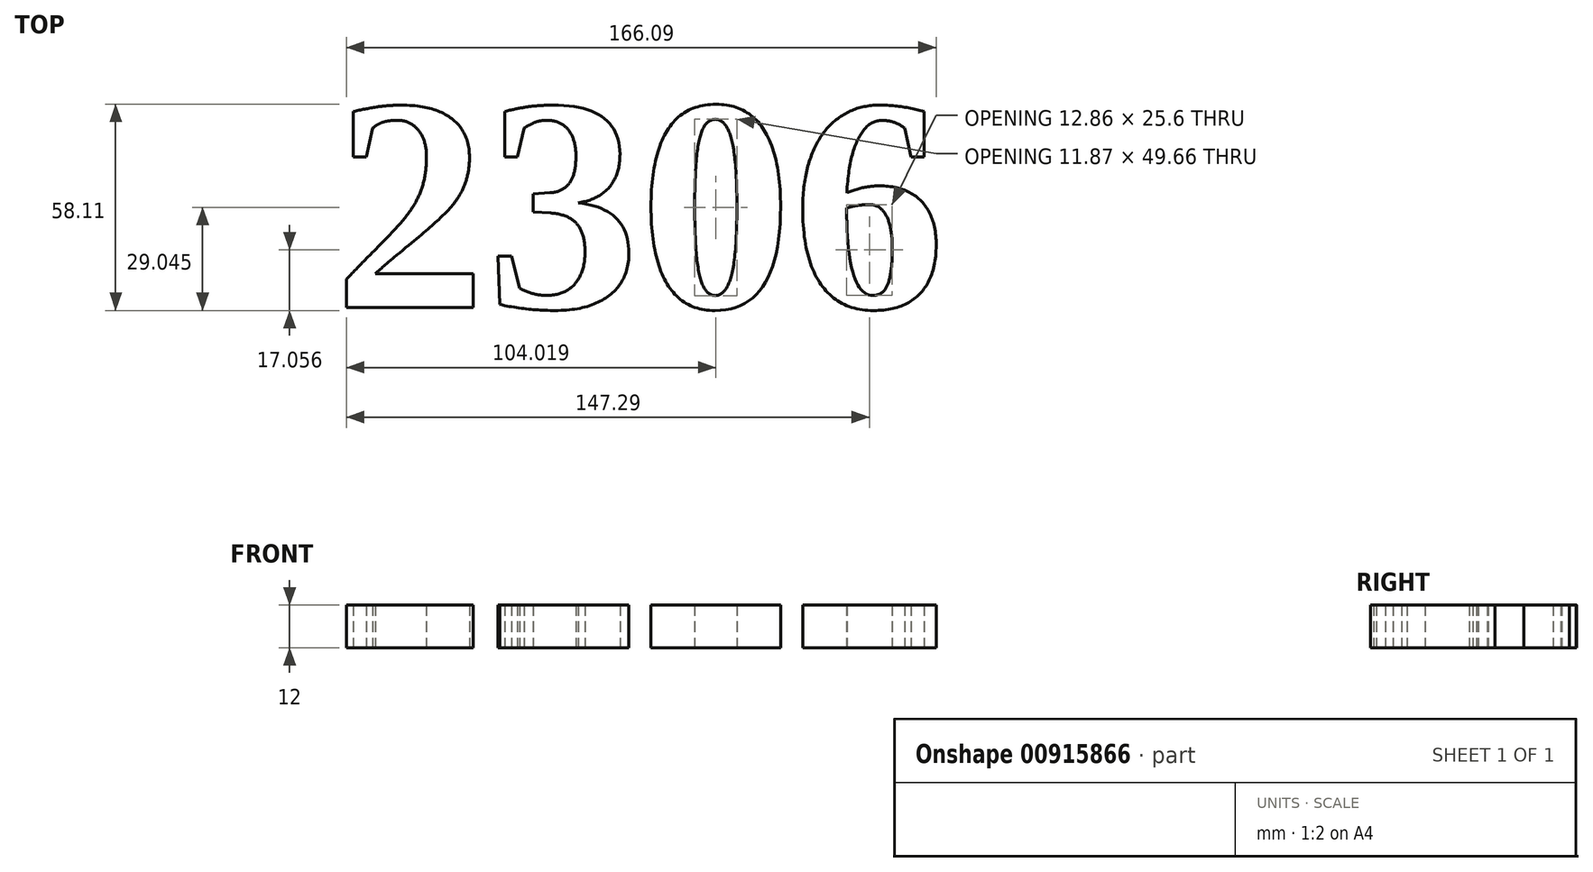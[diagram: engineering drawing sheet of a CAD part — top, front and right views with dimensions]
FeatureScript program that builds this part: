
annotation { "Feature Type Name" : "Feature", "Feature Type Description" : "" }
export const myFeature = defineFeature(function(context is Context, id is Id, definition is map)
    precondition{}
    {
        {
            var Q0;
            Q0=qCreatedBy(makeId("Top.planeOp"),FACE);
            var sketch = newSketch(context, id + "F0", { "sketchPlane" : qUnion([Q0])});
            skText(sketch, "E0", { "text": "2306", "fontName": "Tinos-Bold.ttf"});
            const initialGuessF0  = {"E0": [-0.08754, -0.0306, 1, 0, 0.062]};
            skSetInitialGuess(sketch, initialGuessF0);
            skSolve(sketch);
        }
        {
            var Q0;
            Q0=makeQuery(id+"F0.imprint","IMPRINT",FACE,{"disambiguationData":[TD([[makeQuery(id+"F0.imprint","IMPRINT",EDGE,{"derivedFrom":sQuery(id+"F0.wireOp",EDGE,"E0.sketch_text.stroke-0")}),-1.0]])]});
            var Q1;
            Q1=makeQuery(id+"F0.imprint","IMPRINT",FACE,{"disambiguationData":[TD([[makeQuery(id+"F0.imprint","IMPRINT",EDGE,{"derivedFrom":sQuery(id+"F0.wireOp",EDGE,"E0.sketch_text.stroke-23")}),-1.0]])]});
            var Q2;
            Q2=makeQuery(id+"F0.imprint","IMPRINT",FACE,{"disambiguationData":[TD([[makeQuery(id+"F0.imprint","IMPRINT",EDGE,{"derivedFrom":sQuery(id+"F0.wireOp",EDGE,"E0.sketch_text.stroke-52")}),-1.0]])]});
            var Q3;
            Q3=makeQuery(id+"F0.imprint","IMPRINT",FACE,{"disambiguationData":[TD([[makeQuery(id+"F0.imprint","IMPRINT",EDGE,{"derivedFrom":sQuery(id+"F0.wireOp",EDGE,"E0.sketch_text.stroke-67")}),-1.0]])]});
            extrude(context, id + "F1", {"entities" : qUnion([Q0, Q1, Q2, Q3]), "depth" : 12 * mm, "offsetDistance" : 25 * mm});
        }
    });
